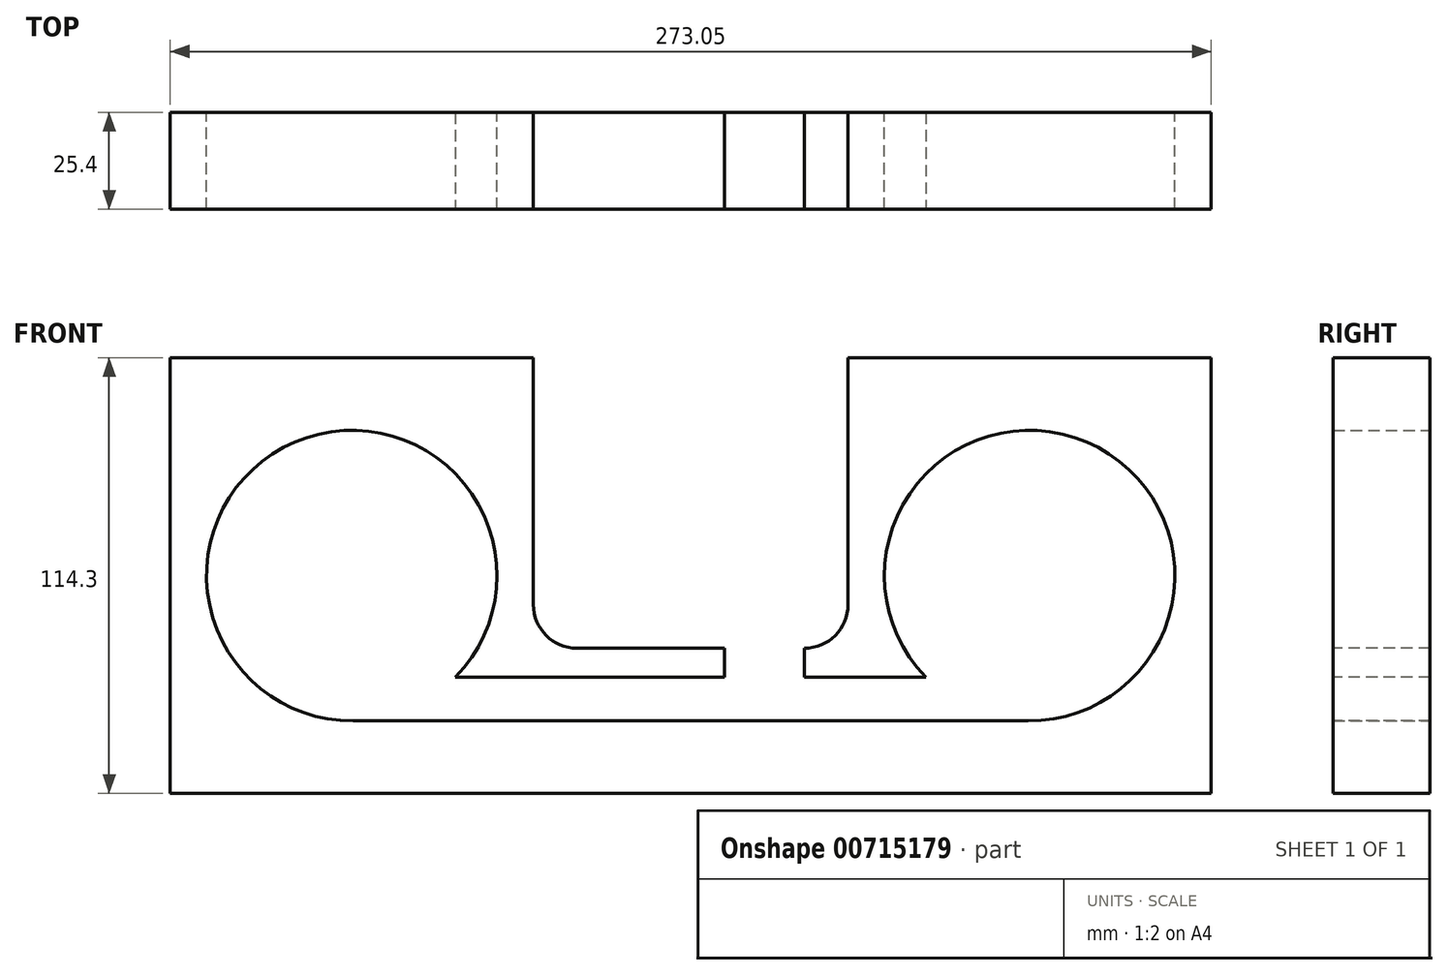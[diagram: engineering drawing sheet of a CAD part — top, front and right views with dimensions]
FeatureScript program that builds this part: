
annotation { "Feature Type Name" : "Feature", "Feature Type Description" : "" }
export const myFeature = defineFeature(function(context is Context, id is Id, definition is map)
    precondition{}
    {
        {
            var Q0;
            Q0=qCreatedBy(makeId("Front.planeOp"),FACE);
            var sketch = newSketch(context, id + "F0", { "sketchPlane" : qUnion([Q0])});
            skLineSegment(sketch, "E0.bottom", {"start": v(0, 0) * mm, "end": v(273.05, 0) * mm});
            skLineSegment(sketch, "E0.top", {"start": v(0, 114.3) * mm, "end": v(273.05, 114.3) * mm});
            skLineSegment(sketch, "E0.left", {"start": v(0, 0) * mm, "end": v(0, 114.3) * mm});
            skLineSegment(sketch, "E0.right", {"start": v(273.05, 0) * mm, "end": v(273.05, 114.3) * mm});
            skCircle(sketch, "E1", {"center": v(47.62, 57.15) * mm, "radius": 38.1 * mm});
            skCircle(sketch, "E2", {"center": v(225.43, 57.15) * mm, "radius": 38.1 * mm});
            skSolve(sketch);
        }
        {
            var Q0;
            Q0 = qSketchRegion(id + "F0", true);
            extrude(context, id + "F1", {"entities" : qUnion([Q0]), "depth" : 25.4 * mm, "offsetDistance" : 25.4 * mm});
        }
        {
            var Q0;
            Q0=makeQuery(id+"F1.opExtrude","CAP_FACE",FACE,{"disambiguationData":[OSD([sQuery(id+"F0.wireOp",EDGE,"E0.bottom"),sQuery(id+"F0.wireOp",EDGE,"E0.top"),sQuery(id+"F0.wireOp",EDGE,"E0.left"),sQuery(id+"F0.wireOp",EDGE,"E0.right"),sQuery(id+"F0.wireOp",EDGE,"E1"),sQuery(id+"F0.wireOp",EDGE,"E2")])],"isStart":false});
            var sketch = newSketch(context, id + "F2", { "sketchPlane" : qUnion([Q0])});
            skLineSegment(sketch, "E3", {"start": v(95.25, 114.3) * mm, "end": v(95.25, 49.53) * mm});
            skLineSegment(sketch, "E4", {"start": v(106.68, 38.1) * mm, "end": v(166.37, 38.1) * mm});
            skLineSegment(sketch, "E5", {"start": v(177.8, 49.53) * mm, "end": v(177.8, 114.3) * mm});
            skPoint(sketch, "E6.visualSharp", {"position": v(95.25, 38.1) * mm});
            skArc(sketch, "E6.filletArc", {"start": v(95.25, 49.53) * mm, "mid": v(98.6, 41.45) * mm, "end": v(106.68, 38.1) * mm});
            skPoint(sketch, "E7.visualSharp", {"position": v(177.8, 38.1) * mm});
            skArc(sketch, "E7.filletArc", {"start": v(166.37, 38.1) * mm, "mid": v(174.45, 41.45) * mm, "end": v(177.8, 49.53) * mm});
            skSolve(sketch);
        }
        {
            var Q0;
            Q0 = qSketchRegion(id + "F2", true);
            var Q1;
            {var subQ1=sQuery(id+"F2.wireOp",EDGE,"E3");Q1=makeQuery(id+"F2.imprint","IMPRINT",FACE,{"disambiguationData":[TD([[makeQuery(id+"F2.imprint","IMPRINT",EDGE,{"derivedFrom":subQ1}),1.0]])]});}
            extrude(context, id + "F3", {"entities" : qUnion([Q0, Q1]), "operationType" : NewBodyOperationType.REMOVE, "oppositeDirection" : true, "depth" : 25.4 * mm, "offsetDistance" : 25.4 * mm});
        }
        {
            var Q0;
            Q0=makeQuery(id+"F1.opExtrude","CAP_FACE",FACE,{"disambiguationData":[OSD([sQuery(id+"F0.wireOp",EDGE,"E0.bottom"),sQuery(id+"F0.wireOp",EDGE,"E0.top"),sQuery(id+"F0.wireOp",EDGE,"E0.left"),sQuery(id+"F0.wireOp",EDGE,"E0.right"),sQuery(id+"F0.wireOp",EDGE,"E1"),sQuery(id+"F0.wireOp",EDGE,"E2")])],"isStart":false});
            var sketch = newSketch(context, id + "F4", { "sketchPlane" : qUnion([Q0])});
            skLineSegment(sketch, "E8", {"start": v(166.37, 38.1) * mm, "end": v(145.38, 38.1) * mm});
            skLineSegment(sketch, "E9", {"start": v(145.38, 38.1) * mm, "end": v(145.38, 30.48) * mm});
            skLineSegment(sketch, "E10", {"start": v(145.38, 30.48) * mm, "end": v(74.84, 30.48) * mm});
            skLineSegment(sketch, "E11", {"start": v(74.84, 30.48) * mm, "end": v(47.26, 19.05) * mm});
            skLineSegment(sketch, "E12", {"start": v(47.26, 19.05) * mm, "end": v(225.06, 19.05) * mm});
            skLineSegment(sketch, "E13", {"start": v(225.06, 19.05) * mm, "end": v(198.21, 30.48) * mm});
            skLineSegment(sketch, "E14", {"start": v(198.21, 30.48) * mm, "end": v(166.37, 30.48) * mm});
            skLineSegment(sketch, "E15", {"start": v(166.37, 30.48) * mm, "end": v(166.37, 38.1) * mm});
            skLineSegment(sketch, "E16", {"start": v(145.38, 38.1) * mm, "end": v(166.37, 38.1) * mm});
            skSolve(sketch);
        }
        {
            var Q0;
            Q0=makeQuery(id+"F4.imprint","IMPRINT",FACE,{"disambiguationData":[TD([[makeQuery(id+"F4.imprint","IMPRINT",EDGE,{"derivedFrom":sQuery(id+"F4.wireOp",EDGE,"E9")}),1.0]])]});
            extrude(context, id + "F5", {"entities" : qUnion([Q0]), "operationType" : NewBodyOperationType.REMOVE, "oppositeDirection" : true, "depth" : 25.4 * mm, "offsetDistance" : 25.4 * mm});
        }
    });
